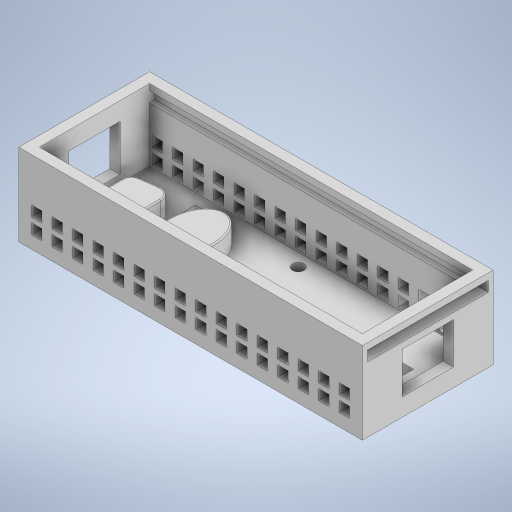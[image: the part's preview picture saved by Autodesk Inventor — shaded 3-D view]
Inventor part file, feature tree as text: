
AUTODESK INVENTOR PART (.ipt)
format: ipt  version: 2024 (Build 280153000, 153)  size: 784,896 bytes
history: native  units: mm
features: sketch x11, extrude x10, fillet x2, shell x1, mirror x1
ambient origin geometry x8: Origin, YZ Plane, XZ Plane, XY Plane, X Axis, Y Axis, Z Axis, Center Point
bodies: Solid1 (feature_tree)
feature tree (25):
  extrude  "Extrusion1"  Depth=67.0mm
  shell  "Shell1"  Thickness=67.0mm
  sketch  "Sketch2"  dims[d3=25.5mm d4=32.0mm d5=0.0mm d6=4.0mm]
  sketch  "Sketch3"  dims[d7=6.8mm d8=21.5mm d9=12.354mm]
  extrude  "Extrusion2"  Depth=32.0mm TaperAngle=0.0deg
  fillet  "Fillet1"  Radius=4.0mm
  extrude  "Extrusion3"  Depth=21.5mm
  fillet  "Fillet2"  Radius=12.354mm
  extrude  "Extrusion4"  Depth=22.5mm
  extrude  "Extrusion5"  Depth=3.5mm
  extrude  "Extrusion6"  Depth=4.3mm
  mirror  "Mirror1"
  sketch  "Sketch10"  dims[d41=21.5mm d42=12.7mm]
  extrude  "Extrusion7"  Depth=0.5mm
  extrude  "Extrusion10"  Depth=12.7mm
  sketch  "Sketch15"  dims[d43=8.7mm d44=16.5mm]
  extrude  "Extrusion13"  Depth=16.5mm
  extrude  "Extrusion14"  Depth=0.5mm
  sketch  "Sketch1"  dims[d0=25.5mm d1=67.0mm d2=67.0mm]
  sketch  "Sketch4"  dims[d10=20.0mm d11=103.0mm d12=8.0mm d13=20.0mm d14=2.0mm d15=4.0mm d16=4.0mm d17=25.0mm d18=14.0mm d19=9.0mm d20=18.0mm d21=6.0mm d22=3.0mm d23=18.0mm d24=9.0mm d25=16.0mm d26=46.0mm d27=6.0mm d28=13.0mm d29=13.0mm d30=22.5mm]
  sketch  "Sketch6"  dims[d31=22.5mm d34=3.5mm]
  sketch  "Sketch7"  dims[d35=4.3mm d36=6.525951mm]
  sketch  "Sketch8"  dims[d37=8.0mm d38=0.0mm d39=0.5mm]
  sketch  "Sketch16"  dims[d45=8.0mm d46=0.0mm d47=0.5mm]
  sketch  "Sketch17"  dims[d59=4.0mm d60=4.0mm d61=5.0mm d62=9.0mm d63=160.0mm d65=8.0mm d66=20.0mm d68=6.0mm d71=4.0mm d72=0.0mm d73=9.0mm d74=7.0mm d75=15.5mm d76=7.0mm d77=4.0mm d78=0.0mm d79=15.5mm d80=7.0mm d81=7.0mm d82=7.0mm d87=4.0mm d88=0.0mm d99=17.0mm d100=66.0mm d101=17.0mm d102=75.0mm d103=20.0mm d105=15.0mm d106=40.0mm d108=15.0mm d112=4.0mm d113=0.0mm d134=22.0mm d135=22.0mm d136=4.0mm d137=4.0mm d138=30.0mm d139=30.0mm d140=97.0mm d141=97.0mm d142=24.0mm d143=98.0mm d144=16.0mm d145=16.0mm d146=10.0mm d147=0.0mm d166=2.0mm d167=2.0mm d168=2.5mm d169=2.5mm d170=130.0mm d171=0.0mm d172=4.5mm d173=4.5mm d177=10.0mm d178=0.0mm d179=32.512mm d151=0.0mm d152=0.0mm d153=0.0mm d154=0.0mm d180=0.5mm d181=0.872665mm d182=0.5mm d183=0.872665mm]
